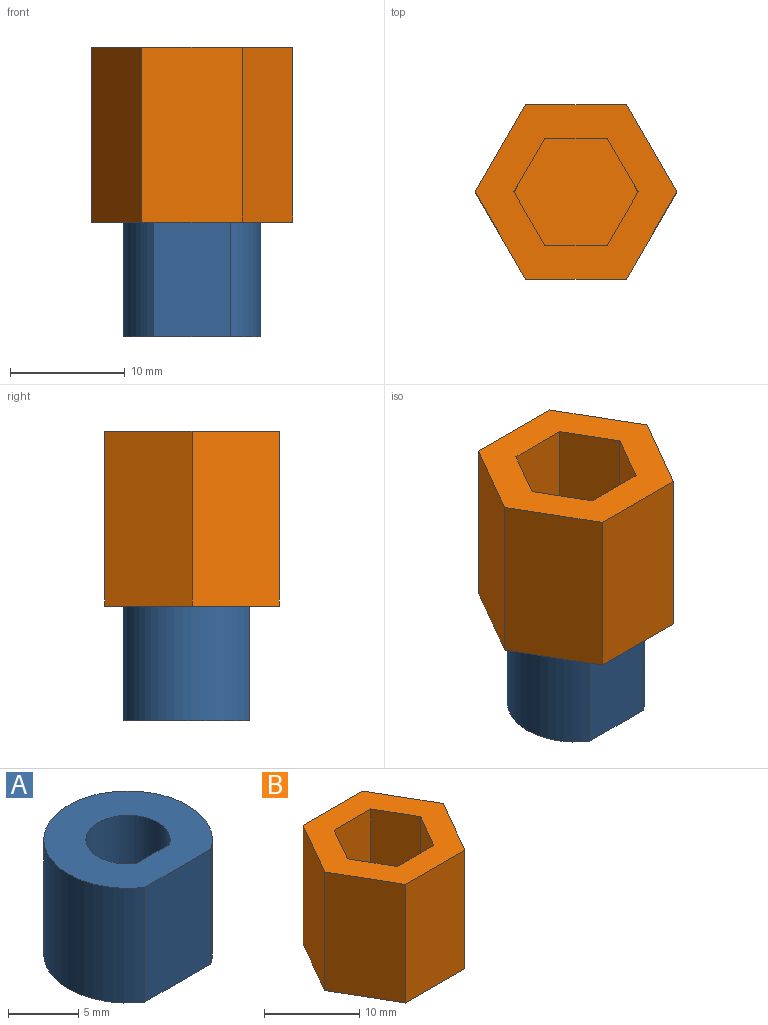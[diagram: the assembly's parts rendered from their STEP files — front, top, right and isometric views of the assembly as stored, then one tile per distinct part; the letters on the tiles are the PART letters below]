
ASSEMBLY  parts=2 mates=1
PART A: 6 faces, bbox 12x11x10 mm
  f0: cylinder r=6mm len=12mm, axis (0,0,-1), area 306.7mm2, adj f3,f4,f5
  f1: plane 10x3.32mm, normal (0,1,0), area 33.2mm2, adj f2,f4,f5
  f2: cylinder r=3mm len=10mm, axis (0,0,-1), area 153.4mm2, adj f1,f4,f5
  f3: plane 10x6.63mm, normal (0,-1,0), area 66.3mm2, adj f0,f4,f5
  f4: plane 12x11mm, normal (0,0,1), area 81.4mm2, adj f0,f1,f2,f3
  f5: plane 12x11mm, normal (0,0,-1), area 81.4mm2, adj f0,f1,f2,f3
PART B: 15 faces, bbox 17.6x15.2x15.2 mm
  f0: plane 12.7x5.43mm, normal (0,-1,0), area 68.9mm2, adj f1,f11,f12,f13
  f1: plane 12.7x4.7mm, normal (-0.87,-0.5,0), area 68.9mm2, adj f0,f2,f12,f13
  f2: plane 12.7x4.7mm, normal (-0.87,0.5,0), area 68.9mm2, adj f1,f3,f12,f13
  f3: plane 12.7x5.43mm, normal (0,1,0), area 68.9mm2, adj f2,f4,f12,f13
  f4: plane 12.7x4.7mm, normal (0.87,0.5,0), area 68.9mm2, adj f3,f11,f12,f13
  f5: plane 15.24x8.8mm, normal (0,1,0), area 134.1mm2, adj f6,f10,f12,f14
  f6: plane 15.24x7.62mm, normal (-0.87,0.5,0), area 134.1mm2, adj f5,f7,f12,f14
  f7: plane 15.24x7.62mm, normal (-0.87,-0.5,0), area 134.1mm2, adj f6,f8,f12,f14
  f8: plane 15.24x8.8mm, normal (0,-1,0), area 134.1mm2, adj f7,f9,f12,f14
  f9: plane 15.24x7.62mm, normal (0.87,-0.5,0), area 134.1mm2, adj f8,f10,f12,f14
  f10: plane 15.24x7.62mm, normal (0.87,0.5,0), area 134.1mm2, adj f5,f9,f12,f14
  f11: plane 12.7x4.7mm, normal (0.87,-0.5,0), area 68.9mm2, adj f0,f4,f12,f13
  f12: plane 17.6x15.24mm, normal (0,0,1), area 124.7mm2, adj f0,f1,f2,f3,f4,f5,f6,f7
  f13: plane 10.85x9.4mm, normal (0,0,1), area 76.5mm2, adj f0,f1,f2,f3,f4,f11
  f14: plane 17.6x15.24mm, normal (0,0,-1), area 201.1mm2, adj f5,f6,f7,f8,f9,f10
PLACE A t=(18.02,-22.24,-14.82)mm
PLACE B t=(18.02,-22.24,-2.28)mm
MATE cylindrical A.f0 <-> B.f14  axis (0,0,1) through (18.02,-22.24,-4.82)mm
